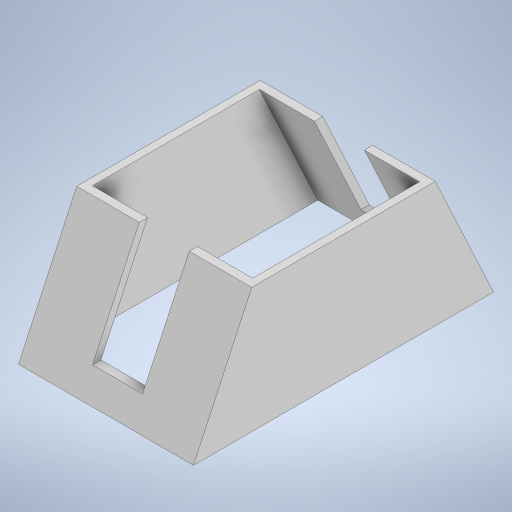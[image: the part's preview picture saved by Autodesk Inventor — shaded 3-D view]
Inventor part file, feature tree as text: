
AUTODESK INVENTOR PART (.ipt)
format: ipt  version: 2023 (Build 270158000, 158)  size: 227,328 bytes
history: native  units: mm
features: extrude x2, sketch x2, shell x1
ambient origin geometry x8: Origin, YZ Plane, XZ Plane, XY Plane, X Axis, Y Axis, Z Axis, Center Point
bodies: Solid1 (feature_tree)
feature tree (5):
  extrude  "Extrusion1"  Depth=120.0mm
  shell  "Shell1"  Thickness=11.34464mm
  extrude  "Extrusion2"  Depth=50.0mm
  sketch  "Sketch1"  dims[d0=120.0mm d1=11.34464mm d2=11.34464mm]
  sketch  "Sketch2"  dims[d3=50.0mm d4=50.0mm d5=70.0mm d6=0.0mm d7=3.0mm d8=10.0mm d9=10.0mm d10=20.0mm d11=40.0mm d12=0.0mm]
